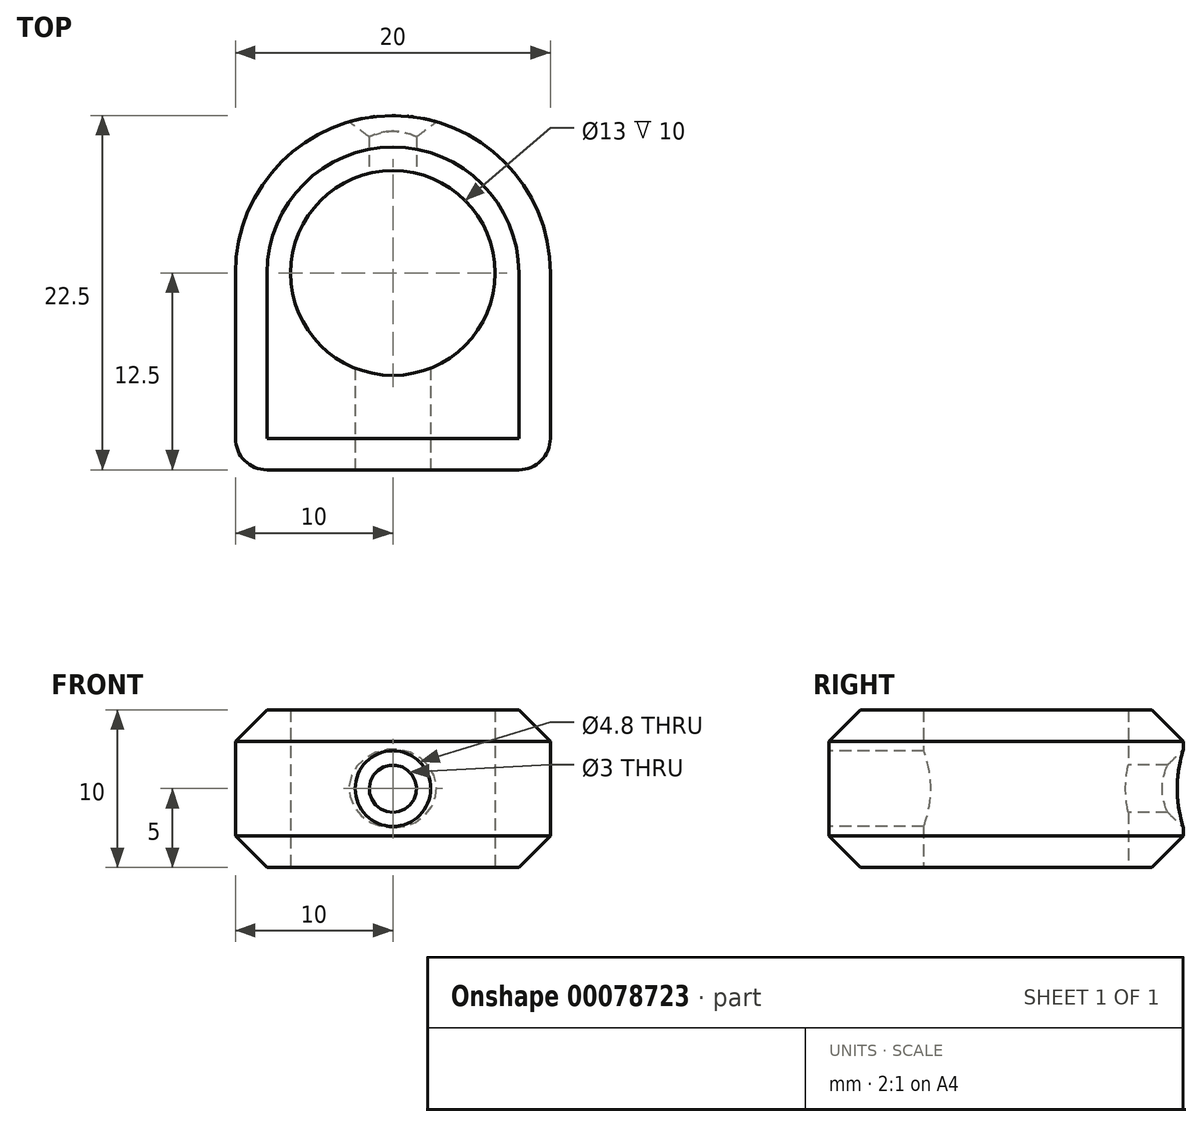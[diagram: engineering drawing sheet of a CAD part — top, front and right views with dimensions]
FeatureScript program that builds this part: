
annotation { "Feature Type Name" : "Feature", "Feature Type Description" : "" }
export const myFeature = defineFeature(function(context is Context, id is Id, definition is map)
    precondition{}
    {
        {
            var Q0;
            Q0=qCreatedBy(makeId("Top.planeOp"),FACE);
            var sketch = newSketch(context, id + "F7", { "sketchPlane" : qUnion([Q0])});
            skCircle(sketch, "E0", {"center": v(0, 0) * mm, "radius": 6.5 * mm});
            skArc(sketch, "E1", {"start": v(10, 0) * mm, "mid": v(0, 10) * mm, "end": v(-10, 0) * mm});
            skLineSegment(sketch, "E2", {"start": v(-10, 0) * mm, "end": v(-10, -12.5) * mm});
            skLineSegment(sketch, "E3", {"start": v(10, 0) * mm, "end": v(10, -12.5) * mm});
            skLineSegment(sketch, "E4", {"start": v(-10, -12.5) * mm, "end": v(10, -12.5) * mm});
            skSolve(sketch);
        }
        {
            var Q0;
            Q0=makeQuery(id+"F7.imprint","IMPRINT",FACE,{"disambiguationData":[TD([[makeQuery(id+"F7.imprint","IMPRINT",EDGE,{"derivedFrom":sQuery(id+"F7.wireOp",EDGE,"E0")}),-1.0]])]});
            extrude(context, id + "F0", {"entities" : qUnion([Q0]), "depth" : 10 * mm});
        }
        {
            var Q0;
            Q0=makeQuery(id+"F0.opExtrude","SWEPT_FACE",FACE,{"disambiguationData":[OSD([sQuery(id+"F7.wireOp",EDGE,"E4")])]});
            var sketch = newSketch(context, id + "F8", { "sketchPlane" : qUnion([Q0])});
            skPoint(sketch, "E5", {"position": v(0, 5) * mm});
            skCircle(sketch, "E6", {"center": v(0, 5) * mm, "radius": 2.4 * mm});
            skSolve(sketch);
        }
        {
            var Q0;
            Q0=makeQuery(id+"F8.imprint","IMPRINT",FACE,{"disambiguationData":[TD([[makeQuery(id+"F8.imprint","IMPRINT",EDGE,{"derivedFrom":sQuery(id+"F8.wireOp",EDGE,"E6")}),1.0]])]});
            extrude(context, id + "F1", {"entities" : qUnion([Q0]), "operationType" : NewBodyOperationType.REMOVE, "oppositeDirection" : true, "depth" : 12.5 * mm});
        }
        {
            var Q0;
            Q0=makeQuery(id+"F0.opExtrude","SWEPT_EDGE",EDGE,{"disambiguationData":[OSD([sQuery(id+"F7.wireOp",EDGE,"E3"),sQuery(id+"F7.wireOp",EDGE,"E4")])]});
            var Q1;
            Q1=makeQuery(id+"F0.opExtrude","SWEPT_EDGE",EDGE,{"disambiguationData":[OSD([sQuery(id+"F7.wireOp",EDGE,"E2"),sQuery(id+"F7.wireOp",EDGE,"E4")])]});
            fillet(context, id + "F2", {"entities" : qUnion([Q0, Q1]), "radius" : 2 * mm, "tangentPropagation" : true, "allowEdgeOverflow" : false});
        }
        {
            var Q0;
            Q0=makeQuery(id+"F0.opExtrude","SWEPT_FACE",FACE,{"disambiguationData":[OSD([sQuery(id+"F7.wireOp",EDGE,"E4")])]});
            var sketch = newSketch(context, id + "F3", { "sketchPlane" : qUnion([Q0])});
            skCircle(sketch, "E7", {"center": v(0, 5) * mm, "radius": 1.5 * mm});
            skSolve(sketch);
        }
        {
            var Q0;
            Q0=makeQuery(id+"F3.imprint","IMPRINT",FACE,{"disambiguationData":[TD([[makeQuery(id+"F3.imprint","IMPRINT",EDGE,{"derivedFrom":sQuery(id+"F3.wireOp",EDGE,"E7")}),1.0]])]});
            extrude(context, id + "F4", {"entities" : qUnion([Q0]), "operationType" : NewBodyOperationType.REMOVE, "oppositeDirection" : true, "depth" : 25 * mm});
        }
        {
            var Q0;
            Q0=makeQuery(id+"F1.boolean.opBoolean","COPY",EDGE,{"derivedFrom":makeQuery(id+"F1.opExtrude","CAP_EDGE",EDGE,{"disambiguationData":[OSD([sQuery(id+"F8.wireOp",EDGE,"E6")])],"isStart":true})});
            var Q1;
            Q1=makeQuery(id+"F4.boolean.opBoolean","INTERSECT",EDGE,{"derivedFrom":[makeQuery(id+"F0.opExtrude","SWEPT_FACE",FACE,{"disambiguationData":[OSD([sQuery(id+"F7.wireOp",EDGE,"E1")])]}),makeQuery(id+"F4.opExtrude","SWEPT_FACE",FACE,{"disambiguationData":[OSD([sQuery(id+"F3.wireOp",EDGE,"E7")])]})]});
            chamfer(context, id + "F5", {"entities" : qUnion([Q0, Q1]), "width" : 1 * mm, "tangentPropagation" : true});
        }
        {
            var Q0;
            Q0=makeQuery(id+"F0.opExtrude","CAP_EDGE",EDGE,{"disambiguationData":[OSD([sQuery(id+"F7.wireOp",EDGE,"E4")])],"isStart":false});
            var Q1;
            Q1=makeQuery(id+"F0.opExtrude","CAP_EDGE",EDGE,{"disambiguationData":[OSD([sQuery(id+"F7.wireOp",EDGE,"E4")])],"isStart":true});
            var Q2;
            {var subQ0=sQuery(id+"F7.wireOp",EDGE,"E4");var subQ1=sQuery(id+"F7.wireOp",EDGE,"E3");Q2=makeQuery(id+"F2.opFillet","BLEND_EDGE",EDGE,{"blendedFrom":[makeQuery(id+"F0.opExtrude","SWEPT_EDGE",EDGE,{"disambiguationData":[OSD([subQ1,subQ0])]}),makeQuery(id+"F0.opExtrude","CAP_FACE",FACE,{"disambiguationData":[OSD([sQuery(id+"F7.wireOp",EDGE,"E0"),sQuery(id+"F7.wireOp",EDGE,"E1"),sQuery(id+"F7.wireOp",EDGE,"E2"),subQ1,subQ0])],"isStart":false})],"blendedInto":[makeQuery(id+"F0.opExtrude","CAP_FACE",FACE,{"disambiguationData":[OSD([sQuery(id+"F7.wireOp",EDGE,"E0"),sQuery(id+"F7.wireOp",EDGE,"E1"),sQuery(id+"F7.wireOp",EDGE,"E2"),subQ1,subQ0])],"isStart":false})]});}
            var Q3;
            {var subQ0=sQuery(id+"F7.wireOp",EDGE,"E4");var subQ1=sQuery(id+"F7.wireOp",EDGE,"E2");Q3=makeQuery(id+"F2.opFillet","BLEND_EDGE",EDGE,{"blendedFrom":[makeQuery(id+"F0.opExtrude","SWEPT_EDGE",EDGE,{"disambiguationData":[OSD([subQ1,subQ0])]}),makeQuery(id+"F0.opExtrude","CAP_FACE",FACE,{"disambiguationData":[OSD([sQuery(id+"F7.wireOp",EDGE,"E0"),sQuery(id+"F7.wireOp",EDGE,"E1"),subQ1,sQuery(id+"F7.wireOp",EDGE,"E3"),subQ0])],"isStart":false})],"blendedInto":[makeQuery(id+"F0.opExtrude","CAP_FACE",FACE,{"disambiguationData":[OSD([sQuery(id+"F7.wireOp",EDGE,"E0"),sQuery(id+"F7.wireOp",EDGE,"E1"),subQ1,sQuery(id+"F7.wireOp",EDGE,"E3"),subQ0])],"isStart":false})]});}
            chamfer(context, id + "F6", {"entities" : qUnion([Q0, Q1, Q2, Q3]), "width" : 2 * mm, "tangentPropagation" : true});
        }
    });
